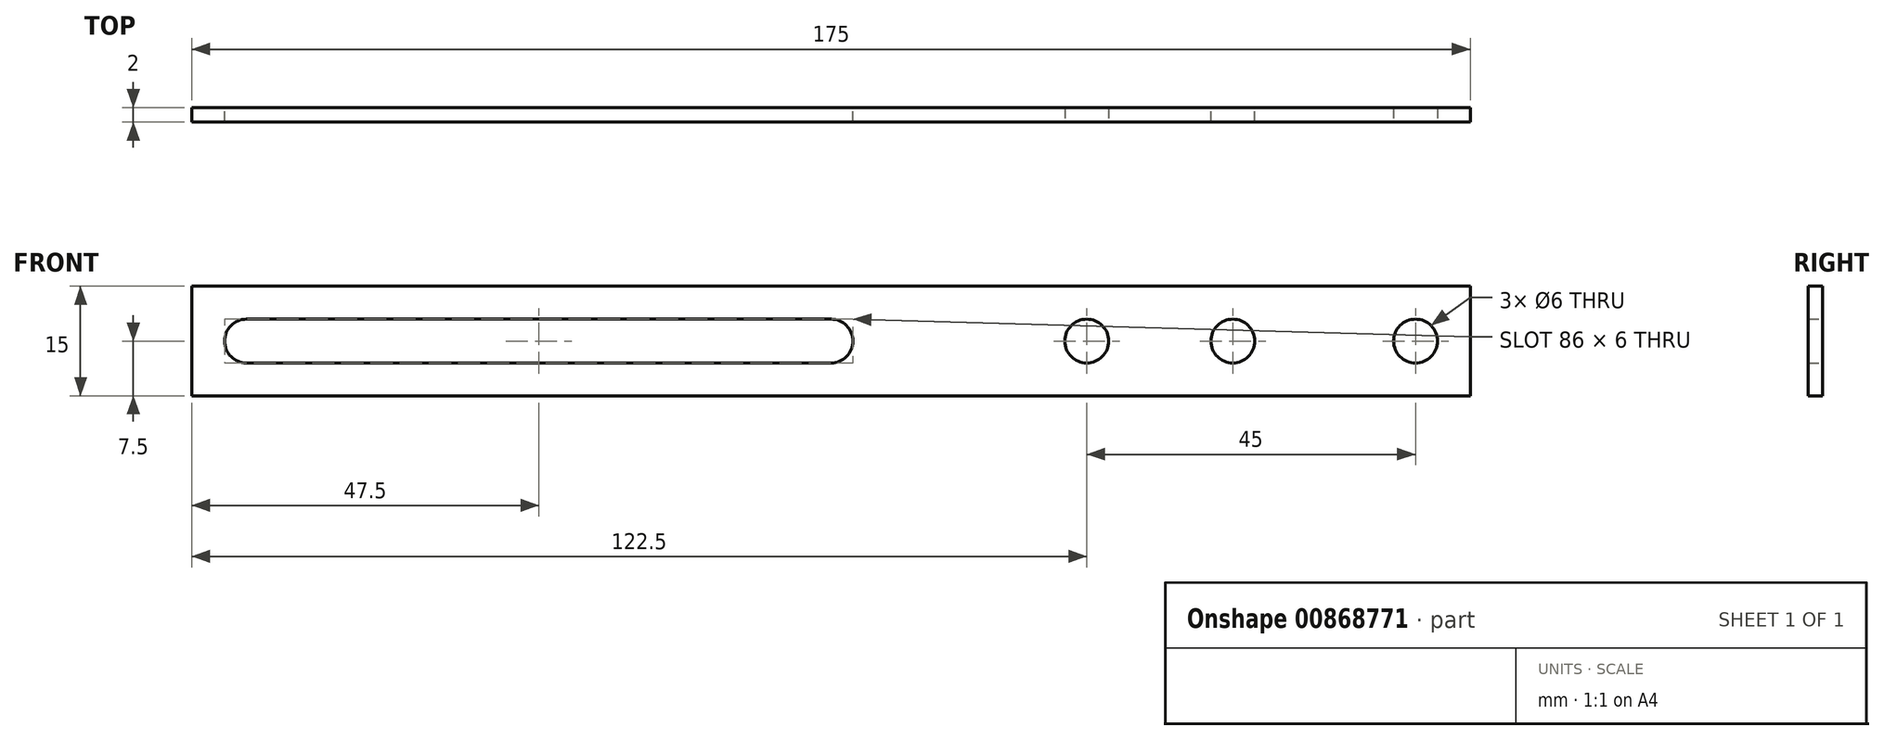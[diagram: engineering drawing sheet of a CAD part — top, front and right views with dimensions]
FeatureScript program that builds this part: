
annotation { "Feature Type Name" : "Feature", "Feature Type Description" : "" }
export const myFeature = defineFeature(function(context is Context, id is Id, definition is map)
    precondition{}
    {
        {
            var Q0;
            Q0=qCreatedBy(makeId("Front.planeOp"),FACE);
            var sketch = newSketch(context, id + "F0", { "sketchPlane" : qUnion([Q0])});
            skLineSegment(sketch, "E0.left", {"start": v(-7.5, -7.5) * mm, "end": v(-7.5, 7.5) * mm});
            skLineSegment(sketch, "E0.right", {"start": v(167.5, -7.5) * mm, "end": v(167.5, 7.5) * mm});
            skCircle(sketch, "E1", {"center": v(135, 0) * mm, "radius": 3 * mm});
            skArc(sketch, "E2", {"start": v(0, 3) * mm, "mid": v(-3, 0) * mm, "end": v(0, -3) * mm});
            skArc(sketch, "E3", {"start": v(80, -3) * mm, "mid": v(83, 0) * mm, "end": v(80, 3) * mm});
            skLineSegment(sketch, "E4", {"start": v(0, 3) * mm, "end": v(80, 3) * mm});
            skLineSegment(sketch, "E5", {"start": v(0, -3) * mm, "end": v(80, -3) * mm});
            skLineSegment(sketch, "E6", {"start": v(-7.5, 7.5) * mm, "end": v(167.5, 7.5) * mm});
            skLineSegment(sketch, "E7", {"start": v(-7.5, -7.5) * mm, "end": v(167.5, -7.5) * mm});
            skSolve(sketch);
        }
        {
            var Q0;
            Q0=makeQuery(id+"F0.imprint","IMPRINT",FACE,{"disambiguationData":[TD([[makeQuery(id+"F0.imprint","IMPRINT",EDGE,{"derivedFrom":sQuery(id+"F0.wireOp",EDGE,"E0.left")}),-1.0]])]});
            extrude(context, id + "F1", {"entities" : qUnion([Q0]), "depth" : 2 * mm, "offsetDistance" : 25 * mm, "symmetric" : true});
        }
        {
            var Q0;
            Q0=makeQuery(id+"F1.opExtrude","CAP_FACE",FACE,{"disambiguationData":[OSD([sQuery(id+"F0.wireOp",EDGE,"E0.left"),sQuery(id+"F0.wireOp",EDGE,"E0.right"),sQuery(id+"F0.wireOp",EDGE,"E1"),sQuery(id+"F0.wireOp",EDGE,"E2"),sQuery(id+"F0.wireOp",EDGE,"E3"),sQuery(id+"F0.wireOp",EDGE,"E4"),sQuery(id+"F0.wireOp",EDGE,"E5"),sQuery(id+"F0.wireOp",EDGE,"E6"),sQuery(id+"F0.wireOp",EDGE,"E7")])],"isStart":false});
            var sketch = newSketch(context, id + "F2", { "sketchPlane" : qUnion([Q0])});
            skCircle(sketch, "E8", {"center": v(160, 0) * mm, "radius": 3 * mm});
            skSolve(sketch);
        }
        {
            var Q0;
            Q0 = qSketchRegion(id + "F2", true);
            extrude(context, id + "F3", {"entities" : qUnion([Q0]), "operationType" : NewBodyOperationType.REMOVE, "endBound" : BoundingType.THROUGH_ALL, "oppositeDirection" : true, "depth" : 25 * mm, "offsetDistance" : 25 * mm});
        }
        {
            var Q0;
            Q0=makeQuery(id+"F1.opExtrude","CAP_FACE",FACE,{"disambiguationData":[OSD([sQuery(id+"F0.wireOp",EDGE,"E0.left"),sQuery(id+"F0.wireOp",EDGE,"E0.right"),sQuery(id+"F0.wireOp",EDGE,"E1"),sQuery(id+"F0.wireOp",EDGE,"E2"),sQuery(id+"F0.wireOp",EDGE,"E3"),sQuery(id+"F0.wireOp",EDGE,"E4"),sQuery(id+"F0.wireOp",EDGE,"E5"),sQuery(id+"F0.wireOp",EDGE,"E6"),sQuery(id+"F0.wireOp",EDGE,"E7")])],"isStart":false});
            var sketch = newSketch(context, id + "F4", { "sketchPlane" : qUnion([Q0])});
            skCircle(sketch, "E9", {"center": v(115, 0) * mm, "radius": 3 * mm});
            skCircle(sketch, "E10.0", {"center": v(135, 0) * mm, "radius": 3 * mm, "construction": true});
            skSolve(sketch);
        }
        {
            var Q0;
            Q0=makeQuery(id+"F4.imprint","IMPRINT",FACE,{"disambiguationData":[TD([[makeQuery(id+"F4.imprint","IMPRINT",EDGE,{"derivedFrom":sQuery(id+"F4.wireOp",EDGE,"E9")}),1.0]])]});
            extrude(context, id + "F5", {"entities" : qUnion([Q0]), "operationType" : NewBodyOperationType.REMOVE, "endBound" : BoundingType.THROUGH_ALL, "oppositeDirection" : true, "depth" : 25 * mm, "offsetDistance" : 25 * mm});
        }
    });
